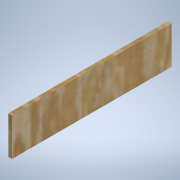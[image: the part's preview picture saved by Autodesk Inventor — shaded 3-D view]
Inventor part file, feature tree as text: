
AUTODESK INVENTOR PART (.ipt)
format: ipt  version: 2021.1 (Build 251245000, 245)  size: 112,128 bytes
history: native  units: mm
features: other x3, extrude x1, sketch x1, reference x1
ambient origin geometry x8: Origin, YZ Plane, XZ Plane, XY Plane, X Axis, Y Axis, Z Axis, Center Point
bodies: Solid1 (feature_tree)
feature tree (6):
  extrude  "Extrusion1"  Depth=270.0mm TaperAngle=0.0deg
  sketch  "Sketch1"  dims[d0=6.35mm d1=270.0mm d2=0.0mm]
  reference  "Reference1"
  other  "<userpath>\Documents\Kerbal Kontroller\v.3.iam"
  other  "v.3.iam"
  other  "Bottom:1"
